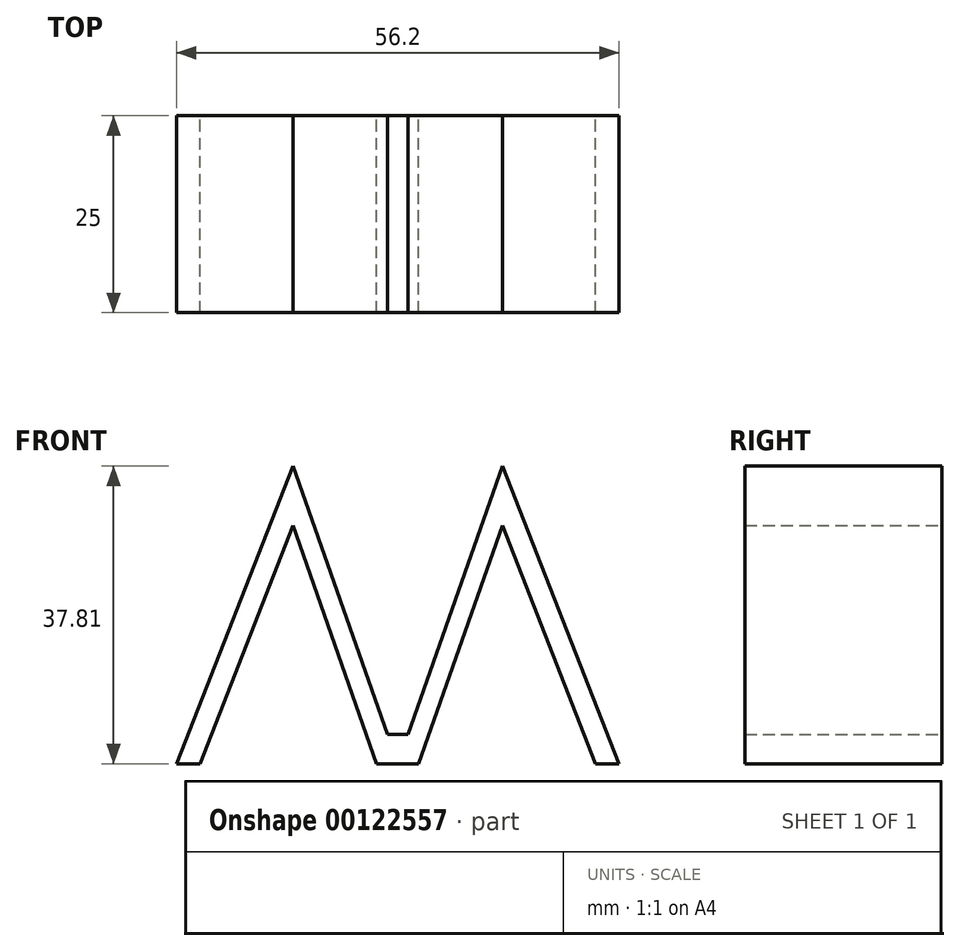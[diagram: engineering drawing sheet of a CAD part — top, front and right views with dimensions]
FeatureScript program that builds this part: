
annotation { "Feature Type Name" : "Feature", "Feature Type Description" : "" }
export const myFeature = defineFeature(function(context is Context, id is Id, definition is map)
    precondition{}
    {
        {
            var Q0;
            Q0=qCreatedBy(makeId("Front.planeOp"),FACE);
            var sketch = newSketch(context, id + "F0", { "sketchPlane" : qUnion([Q0])});
            skLineSegment(sketch, "E0", {"start": v(-28.1, 0) * mm, "end": v(-13.3, 37.8) * mm});
            skLineSegment(sketch, "E1", {"start": v(-13.3, 37.8) * mm, "end": v(0, 0) * mm});
            skLineSegment(sketch, "E2", {"start": v(-28.1, 0) * mm, "end": v(-25.14, 0) * mm});
            skLineSegment(sketch, "E3", {"start": v(-25.14, 0) * mm, "end": v(-13.3, 30.24) * mm});
            skLineSegment(sketch, "E4", {"start": v(-13.3, 30.24) * mm, "end": v(-2.66, 0) * mm});
            skLineSegment(sketch, "E5", {"start": v(-2.66, 0) * mm, "end": v(0, 0) * mm});
            skLineSegment(sketch, "E6.MirrorCS", {"start": v(28.1, 0) * mm, "end": v(25.14, 0) * mm});
            skLineSegment(sketch, "E7.MirrorCS", {"start": v(2.66, 0) * mm, "end": v(0, 0) * mm});
            skLineSegment(sketch, "E8.MirrorCS", {"start": v(28.1, 0) * mm, "end": v(13.3, 37.8) * mm});
            skLineSegment(sketch, "E9.MirrorCS", {"start": v(13.3, 37.8) * mm, "end": v(0, 0) * mm});
            skLineSegment(sketch, "E10.MirrorCS", {"start": v(25.14, 0) * mm, "end": v(13.3, 30.24) * mm});
            skLineSegment(sketch, "E11.MirrorCS", {"start": v(13.3, 30.24) * mm, "end": v(2.66, 0) * mm});
            skSolve(sketch);
        }
        {
            var Q0;
            Q0=makeQuery(id+"F0.imprint","IMPRINT",FACE,{"disambiguationData":[TD([[makeQuery(id+"F0.imprint","IMPRINT",EDGE,{"derivedFrom":sQuery(id+"F0.wireOp",EDGE,"E0")}),-1.0]])]});
            var Q1;
            Q1=makeQuery(id+"F0.imprint","IMPRINT",FACE,{"disambiguationData":[TD([[makeQuery(id+"F0.imprint","IMPRINT",EDGE,{"derivedFrom":sQuery(id+"F0.wireOp",EDGE,"E6.MirrorCS")}),-1.0]])]});
            extrude(context, id + "F1", {"entities" : qUnion([Q0, Q1]), "depth" : 25 * mm});
        }
        {
            var Q0;
            Q0=makeQuery(id+"F1.opExtrude","CAP_FACE",FACE,{"disambiguationData":[OSD([sQuery(id+"F0.wireOp",EDGE,"E0"),sQuery(id+"F0.wireOp",EDGE,"E1"),sQuery(id+"F0.wireOp",EDGE,"E2"),sQuery(id+"F0.wireOp",EDGE,"E3"),sQuery(id+"F0.wireOp",EDGE,"E4"),sQuery(id+"F0.wireOp",EDGE,"E5")])],"isStart":false});
            var sketch = newSketch(context, id + "F2", { "sketchPlane" : qUnion([Q0])});
            skPoint(sketch, "E12.0", {"position": v(2.66, 0) * mm});
            skPoint(sketch, "E13.0", {"position": v(-2.66, 0) * mm});
            skLineSegment(sketch, "E14.bottom", {"start": v(-2.66, 0) * mm, "end": v(2.66, 0) * mm});
            skLineSegment(sketch, "E14.top", {"start": v(-2.66, 3.75) * mm, "end": v(2.66, 3.75) * mm});
            skLineSegment(sketch, "E14.left", {"start": v(-2.66, 0) * mm, "end": v(-2.66, 3.75) * mm});
            skLineSegment(sketch, "E14.right", {"start": v(2.66, 0) * mm, "end": v(2.66, 3.75) * mm});
            skSolve(sketch);
        }
        {
            var Q0;
            Q0 = qSketchRegion(id + "F2", true);
            extrude(context, id + "F3", {"entities" : qUnion([Q0]), "operationType" : NewBodyOperationType.ADD, "oppositeDirection" : true, "depth" : 25 * mm});
        }
    });
